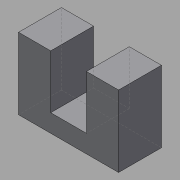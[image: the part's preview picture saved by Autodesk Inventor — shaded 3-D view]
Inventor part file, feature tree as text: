
AUTODESK INVENTOR PART (.ipt)
format: ipt  version: 2015 (Build 190159000, 159)  size: 80,896 bytes
history: native  units: mm
features: extrude x2, sketch x2
ambient origin geometry x8: Origin, YZ Plane, XZ Plane, XY Plane, X Axis, Y Axis, Z Axis, Center Point
bodies: Solid1 (feature_tree)
feature tree (4):
  extrude  "Extrusion1"  Depth=6.0mm
  extrude  "Extrusion2"  Depth=7.5mm TaperAngle=0.0deg
  sketch  "Sketch1"  dims[d0=14.0mm d1=6.0mm]
  sketch  "Sketch2"  dims[d2=10.0mm d3=0.0mm d6=7.5mm d7=0.0mm]
